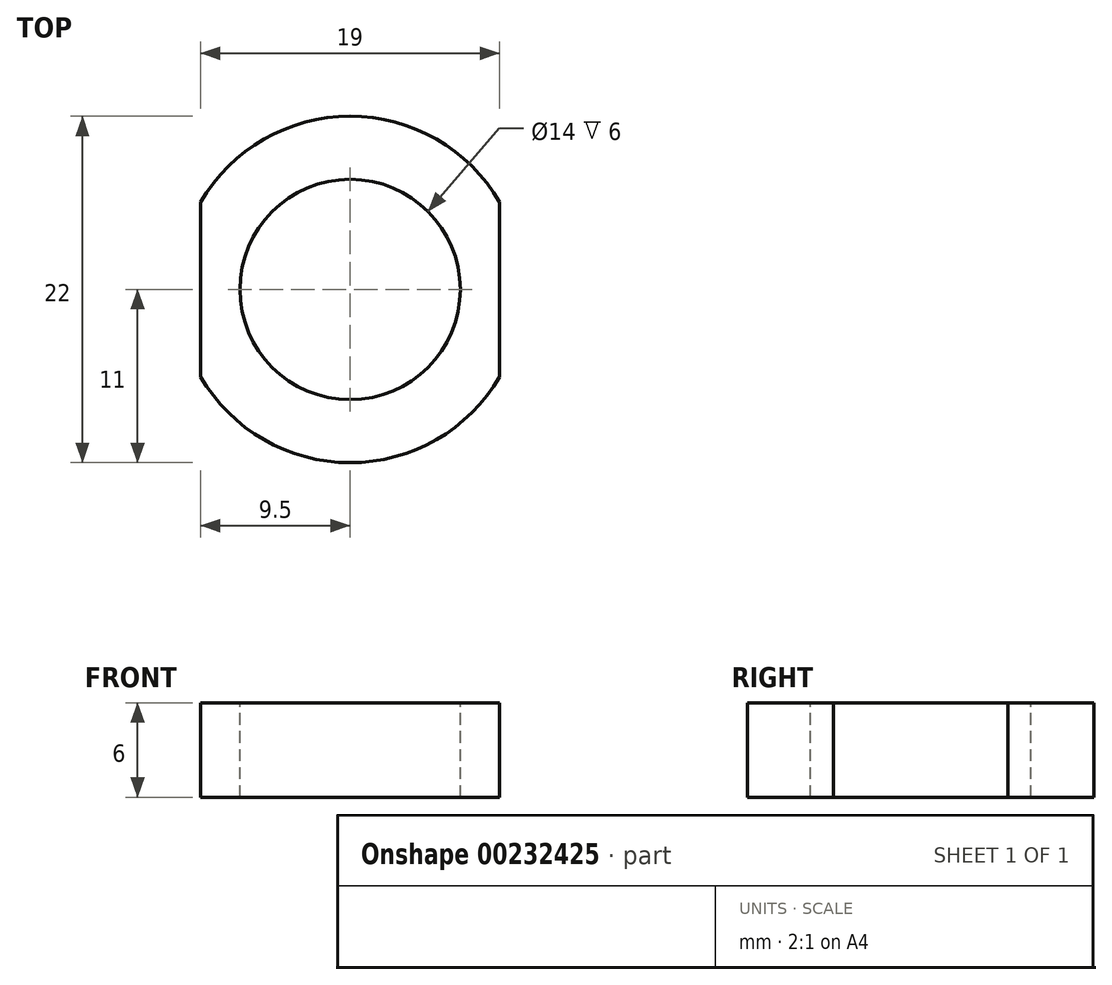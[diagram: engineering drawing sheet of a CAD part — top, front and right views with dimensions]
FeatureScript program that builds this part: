
annotation { "Feature Type Name" : "Feature", "Feature Type Description" : "" }
export const myFeature = defineFeature(function(context is Context, id is Id, definition is map)
    precondition{}
    {
        {
            var Q0;
            Q0=qCreatedBy(makeId("Top.planeOp"),FACE);
            var sketch = newSketch(context, id + "F0", { "sketchPlane" : qUnion([Q0])});
            skArc(sketch, "E0", {"start": v(-9.5, -5.55) * mm, "mid": v(0, -11) * mm, "end": v(9.5, -5.55) * mm});
            skLineSegment(sketch, "E1.left", {"start": v(-9.5, 5.55) * mm, "end": v(-9.5, -5.55) * mm});
            skLineSegment(sketch, "E1.right", {"start": v(9.5, 5.55) * mm, "end": v(9.5, -5.55) * mm});
            skPoint(sketch, "E1.bottom.start.orphan", {"position": v(-9.5, 13.08) * mm});
            skPoint(sketch, "E1.top.start.orphan", {"position": v(-9.5, -13.08) * mm});
            skPoint(sketch, "E2.orphan", {"position": v(9.5, -13.08) * mm});
            skArc(sketch, "E3.trimOffspring", {"start": v(9.5, 5.55) * mm, "mid": v(0, 11) * mm, "end": v(-9.5, 5.55) * mm});
            skPoint(sketch, "E4.orphan", {"position": v(9.5, 13.08) * mm});
            skSolve(sketch);
        }
        {
            var Q0;
            Q0=makeQuery(id+"F0.imprint","IMPRINT",FACE,{"disambiguationData":[TD([[makeQuery(id+"F0.imprint","IMPRINT",EDGE,{"derivedFrom":sQuery(id+"F0.wireOp",EDGE,"E0")}),1.0]])]});
            extrude(context, id + "F1", {"entities" : qUnion([Q0]), "endBound" : BoundingType.SYMMETRIC, "depth" : 6 * mm});
        }
        {
            var Q0;
            Q0=makeQuery(id+"F1.opExtrude","CAP_FACE",FACE,{"disambiguationData":[OSD([sQuery(id+"F0.wireOp",EDGE,"E0"),sQuery(id+"F0.wireOp",EDGE,"E1.left"),sQuery(id+"F0.wireOp",EDGE,"E1.right"),sQuery(id+"F0.wireOp",EDGE,"E3.trimOffspring")])],"isStart":false});
            var sketch = newSketch(context, id + "F2", { "sketchPlane" : qUnion([Q0])});
            skPoint(sketch, "E5", {"position": v(0, 0) * mm});
            skSolve(sketch);
        }
        {
            var Q0;
            Q0=sQuery(id+"F2.wireOp",VERTEX,"E5");
            var Q1;
            Q1=makeQuery(id+"F1.opExtrude","SWEPT_BODY",BODY,{"disambiguationData":[OSD([sQuery(id+"F0.wireOp",EDGE,"E0"),sQuery(id+"F0.wireOp",EDGE,"E1.left"),sQuery(id+"F0.wireOp",EDGE,"E1.right"),sQuery(id+"F0.wireOp",EDGE,"E3.trimOffspring")])]});
            hole(context, id + "F3", {"style" : HoleStyle.SIMPLE, "endStyle" : HoleEndStyle.THROUGH, "standardTappedOrClearance" : lookupTablePath({ "standard" : "ISO", "engagement" : "75%", "pitch" : "2 mm", "size" : "M16", "type" : "Tapped" }), "standardBlindInLast" : lookupTablePath({ "standard" : "ISO", "engagement" : "75%", "pitch" : "2 mm", "size" : "M16", "type" : "Tapped" }), "holeDiameter" : 14 * mm, "startFromSketch" : true, "locations" : qUnion([Q0]), "scope" : qUnion([Q1]), "isTappedThrough" : true, "majorDiameter" : 16 * mm, "showTappedDepth" : true});
        }
    });
